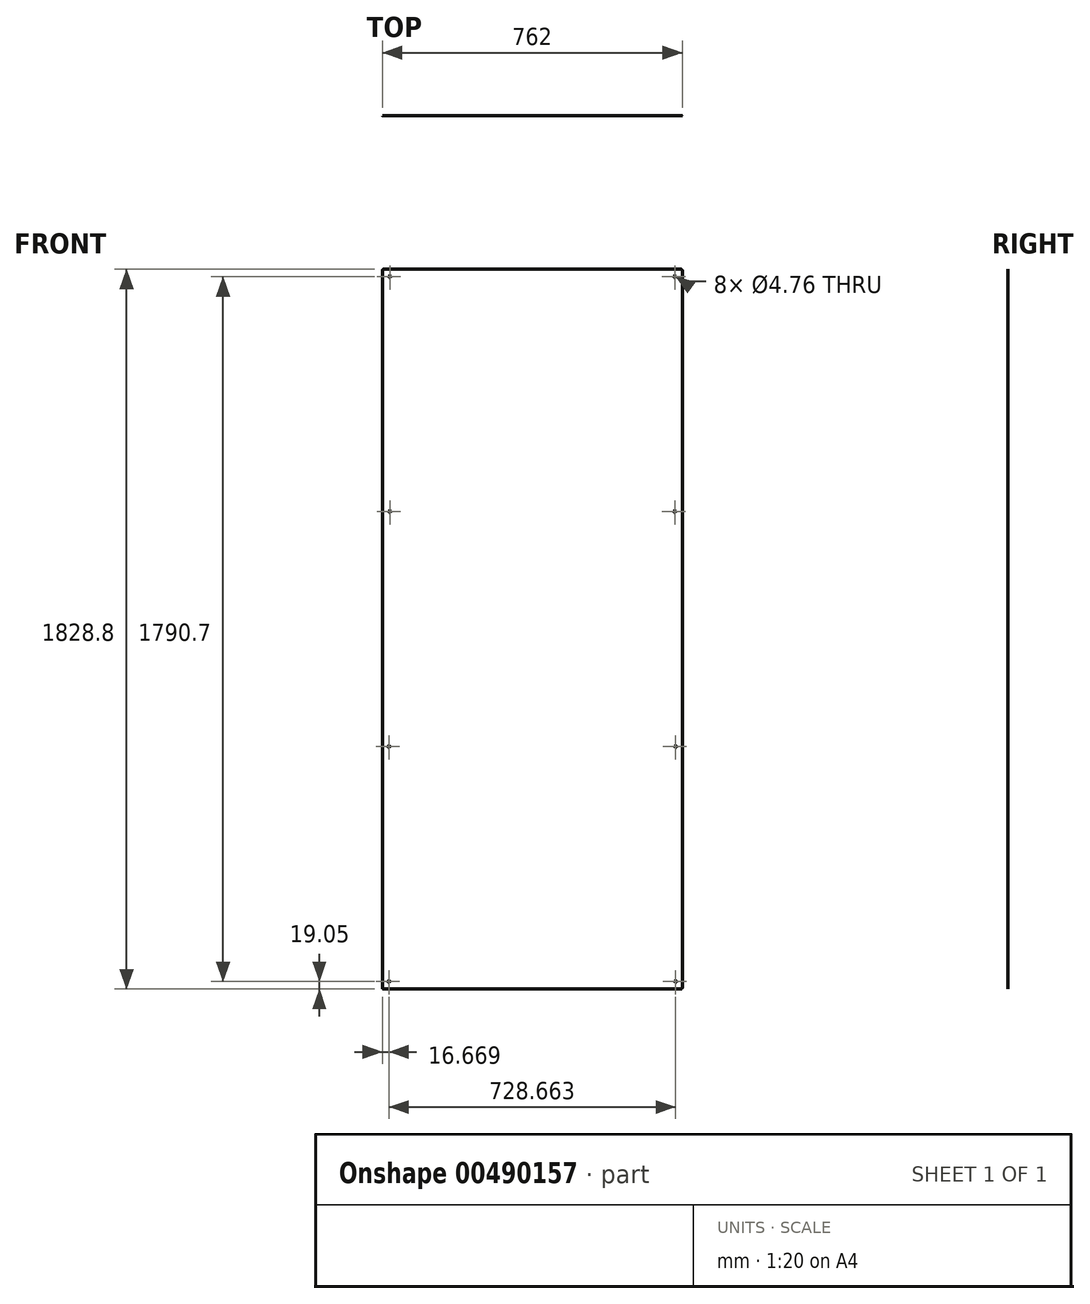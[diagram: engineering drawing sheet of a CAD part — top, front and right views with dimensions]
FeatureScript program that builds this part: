
annotation { "Feature Type Name" : "Feature", "Feature Type Description" : "" }
export const myFeature = defineFeature(function(context is Context, id is Id, definition is map)
    precondition{}
    {
        {
            var Q0;
            Q0=qCreatedBy(makeId("Front.planeOp"),FACE);
            var sketch = newSketch(context, id + "F0", { "sketchPlane" : qUnion([Q0])});
            skLineSegment(sketch, "E0.bottom", {"start": v(377.83, -914.4) * mm, "end": v(-377.82, -914.4) * mm});
            skLineSegment(sketch, "E0.top", {"start": v(377.83, 914.4) * mm, "end": v(-377.83, 914.4) * mm});
            skLineSegment(sketch, "E0.left", {"start": v(381, -911.22) * mm, "end": v(381, 911.23) * mm});
            skLineSegment(sketch, "E0.right", {"start": v(-381, -911.23) * mm, "end": v(-381, 911.22) * mm});
            skPoint(sketch, "E0.middle", {"position": v(0, 0) * mm});
            skPoint(sketch, "E1.visualSharp", {"position": v(-381, 914.4) * mm});
            skArc(sketch, "E1.filletArc", {"start": v(-377.83, 914.4) * mm, "mid": v(-380.07, 913.47) * mm, "end": v(-381, 911.22) * mm});
            skPoint(sketch, "E2.visualSharp", {"position": v(381, 914.4) * mm});
            skArc(sketch, "E2.filletArc", {"start": v(381, 911.23) * mm, "mid": v(380.07, 913.47) * mm, "end": v(377.83, 914.4) * mm});
            skPoint(sketch, "E3.visualSharp", {"position": v(381, -914.4) * mm});
            skArc(sketch, "E3.filletArc", {"start": v(377.83, -914.4) * mm, "mid": v(380.07, -913.47) * mm, "end": v(381, -911.22) * mm});
            skPoint(sketch, "E4.visualSharp", {"position": v(-381, -914.4) * mm});
            skArc(sketch, "E4.filletArc", {"start": v(-381, -911.23) * mm, "mid": v(-380.07, -913.47) * mm, "end": v(-377.82, -914.4) * mm});
            skSolve(sketch);
        }
        {
            var Q0;
            Q0 = qSketchRegion(id + "F0", true);
            extrude(context, id + "F1", {"entities" : qUnion([Q0]), "depth" : 1 / 406.4 * mm});
        }
        {
            var Q0;
            Q0=makeQuery(id+"F1.opExtrude","CAP_FACE",FACE,{"disambiguationData":[OSD([sQuery(id+"F0.wireOp",EDGE,"E0.bottom"),sQuery(id+"F0.wireOp",EDGE,"E0.top"),sQuery(id+"F0.wireOp",EDGE,"E0.left"),sQuery(id+"F0.wireOp",EDGE,"E0.right"),sQuery(id+"F0.wireOp",EDGE,"E1.filletArc"),sQuery(id+"F0.wireOp",EDGE,"E2.filletArc"),sQuery(id+"F0.wireOp",EDGE,"E3.filletArc"),sQuery(id+"F0.wireOp",EDGE,"E4.filletArc")])],"isStart":false});
            var sketch = newSketch(context, id + "F2", { "sketchPlane" : qUnion([Q0])});
            skLineSegment(sketch, "E5", {"start": v(-361.95, 895.35) * mm, "end": v(-361.95, 914.4) * mm, "construction": true});
            skLineSegment(sketch, "E6", {"start": v(-361.95, 895.35) * mm, "end": v(-381, 895.35) * mm, "construction": true});
            skCircle(sketch, "E7", {"center": v(-361.95, 895.35) * mm, "radius": 2.38 * mm});
            skCircle(sketch, "E8", {"center": v(-361.95, 298.45) * mm, "radius": 2.38 * mm});
            skLineSegment(sketch, "E9", {"start": v(-361.95, 895.35) * mm, "end": v(-361.95, 298.45) * mm, "construction": true});
            skLineSegment(sketch, "E10", {"start": v(-361.95, 298.45) * mm, "end": v(-364.33, -298.45) * mm, "construction": true});
            skCircle(sketch, "E11", {"center": v(-364.33, -298.45) * mm, "radius": 2.38 * mm});
            skCircle(sketch, "E12", {"center": v(-364.33, -895.35) * mm, "radius": 2.38 * mm});
            skLineSegment(sketch, "E13", {"start": v(-364.33, -298.45) * mm, "end": v(-364.33, -895.35) * mm, "construction": true});
            skLineSegment(sketch, "E14", {"start": v(-364.33, -895.35) * mm, "end": v(-364.33, -914.4) * mm, "construction": true});
            skCircle(sketch, "E15.MirrorC", {"center": v(361.95, 895.35) * mm, "radius": 2.38 * mm});
            skCircle(sketch, "E16.MirrorC", {"center": v(364.33, -895.35) * mm, "radius": 2.38 * mm});
            skCircle(sketch, "E17.MirrorC", {"center": v(361.95, 298.45) * mm, "radius": 2.38 * mm});
            skCircle(sketch, "E18.MirrorC", {"center": v(364.33, -298.45) * mm, "radius": 2.38 * mm});
            skLineSegment(sketch, "E19.MirrorCS", {"start": v(364.33, -895.35) * mm, "end": v(364.33, -914.4) * mm, "construction": true});
            skLineSegment(sketch, "E20.MirrorCS", {"start": v(361.95, 895.35) * mm, "end": v(381, 895.35) * mm, "construction": true});
            skLineSegment(sketch, "E21.MirrorCS", {"start": v(361.95, 895.35) * mm, "end": v(361.95, 914.4) * mm, "construction": true});
            skLineSegment(sketch, "E22.MirrorCS", {"start": v(361.95, 298.45) * mm, "end": v(364.33, -298.45) * mm, "construction": true});
            skLineSegment(sketch, "E23.MirrorCS", {"start": v(361.95, 895.35) * mm, "end": v(361.95, 298.45) * mm, "construction": true});
            skLineSegment(sketch, "E24.MirrorCS", {"start": v(364.33, -298.45) * mm, "end": v(364.33, -895.35) * mm, "construction": true});
            skSolve(sketch);
        }
        {
            var Q0;
            Q0 = qSketchRegion(id + "F2", true);
            extrude(context, id + "F3", {"entities" : qUnion([Q0]), "operationType" : NewBodyOperationType.REMOVE, "endBound" : BoundingType.THROUGH_ALL, "oppositeDirection" : true, "depth" : 25.4 * mm});
        }
    });
